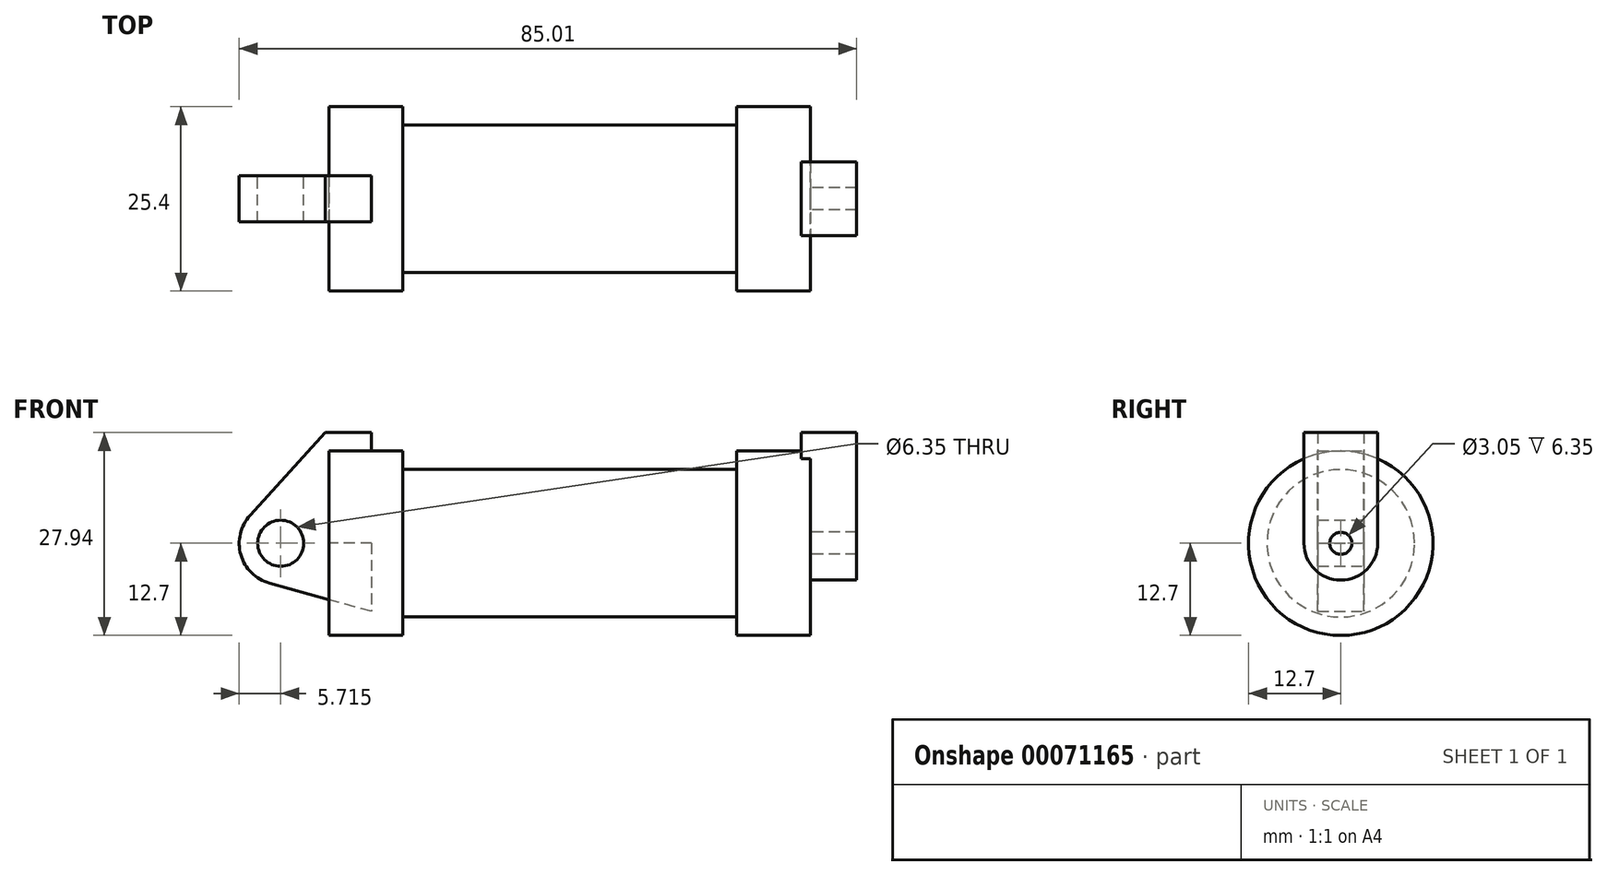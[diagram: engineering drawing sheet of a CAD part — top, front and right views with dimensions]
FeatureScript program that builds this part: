
annotation { "Feature Type Name" : "Feature", "Feature Type Description" : "" }
export const myFeature = defineFeature(function(context is Context, id is Id, definition is map)
    precondition{}
    {
        {
            var Q0;
            Q0=qCreatedBy(makeId("Front.planeOp"),FACE);
            var sketch = newSketch(context, id + "F0", { "sketchPlane" : qUnion([Q0])});
            skLineSegment(sketch, "E0", {"start": v(0, 0) * mm, "end": v(0, 12.7) * mm});
            skLineSegment(sketch, "E1", {"start": v(0, 12.7) * mm, "end": v(10.16, 12.7) * mm});
            skLineSegment(sketch, "E2", {"start": v(10.16, 12.7) * mm, "end": v(10.16, 10.16) * mm});
            skLineSegment(sketch, "E3", {"start": v(10.16, 10.16) * mm, "end": v(56.13, 10.16) * mm});
            skLineSegment(sketch, "E4", {"start": v(56.13, 10.16) * mm, "end": v(56.13, 12.7) * mm});
            skLineSegment(sketch, "E5", {"start": v(56.13, 12.7) * mm, "end": v(66.3, 12.7) * mm});
            skLineSegment(sketch, "E6", {"start": v(66.3, 12.7) * mm, "end": v(66.3, 0) * mm});
            skLineSegment(sketch, "E7", {"start": v(66.3, 0) * mm, "end": v(0, 0) * mm});
            skLineSegment(sketch, "E8", {"start": v(5.84, 15.24) * mm, "end": v(-0.5, 15.24) * mm});
            skLineSegment(sketch, "E9", {"start": v(-0.5, 15.24) * mm, "end": v(-10.88, 3.85) * mm});
            skLineSegment(sketch, "E10", {"start": v(0, 0) * mm, "end": v(-6.65, 0) * mm});
            skCircle(sketch, "E11", {"center": v(-6.65, 0) * mm, "radius": 5.72 * mm});
            skCircle(sketch, "E12", {"center": v(-6.65, 0) * mm, "radius": 3.18 * mm});
            skLineSegment(sketch, "E13", {"start": v(5.84, 15.24) * mm, "end": v(5.84, -9.4) * mm});
            skLineSegment(sketch, "E14", {"start": v(5.84, -9.4) * mm, "end": v(-8.18, -5.5) * mm});
            skSolve(sketch);
        }
        {
            var Q0;
            {var subQ0=sQuery(id+"F0.wireOp",EDGE,"E2");Q0=makeQuery(id+"F0.imprint","IMPRINT",FACE,{"disambiguationData":[TD([[makeQuery(id+"F0.imprint","IMPRINT",EDGE,{"derivedFrom":subQ0}),-1.0]])]});}
            var Q1;
            {var subQ0=sQuery(id+"F0.wireOp",EDGE,"E0");Q1=makeQuery(id+"F0.imprint","IMPRINT",FACE,{"disambiguationData":[TD([[makeQuery(id+"F0.imprint","IMPRINT",EDGE,{"derivedFrom":subQ0}),-1.0]])]});}
            var Q2;
            Q2=sQuery(id+"F0.wireOp",EDGE,"E7");
            revolve(context, id + "F1", {"entities" : qUnion([Q0, Q1]), "axis" : qUnion([Q2]), "revolveType" : RevolveType.FULL});
        }
        {
            var Q0;
            {var subQ3=sQuery(id+"F0.wireOp",EDGE,"E0");Q0=makeQuery(id+"F0.imprint","IMPRINT",FACE,{"disambiguationData":[TD([[makeQuery(id+"F0.imprint","IMPRINT",EDGE,{"derivedFrom":subQ3}),1.0]])]});}
            var Q1;
            {var subQ0=sQuery(id+"F0.wireOp",EDGE,"E14");Q1=makeQuery(id+"F0.imprint","IMPRINT",FACE,{"disambiguationData":[TD([[makeQuery(id+"F0.imprint","IMPRINT",EDGE,{"derivedFrom":subQ0}),-1.0]])]});}
            var Q2;
            {var subQ4=sQuery(id+"F0.wireOp",EDGE,"E12");Q2=makeQuery(id+"F0.imprint","IMPRINT",FACE,{"disambiguationData":[TD([[makeQuery(id+"F0.imprint","IMPRINT",EDGE,{"derivedFrom":subQ4}),-1.0]])]});}
            extrude(context, id + "F2", {"entities" : qUnion([Q0, Q1, Q2]), "depth" : 3.17 * mm, "hasSecondDirection" : true, "secondDirectionOppositeDirection" : true, "secondDirectionDepth" : 3.17 * mm});
        }
        {
            var Q0;
            Q0=makeQuery(id+"F1.opRevolve","SWEPT_FACE",FACE,{"disambiguationData":[OSD([sQuery(id+"F0.wireOp",EDGE,"E6")])]});
            var sketch = newSketch(context, id + "F3", { "sketchPlane" : qUnion([Q0])});
            skCircle(sketch, "E15", {"center": v(0, 0) * mm, "radius": 5.08 * mm});
            skCircle(sketch, "E16", {"center": v(0, 0) * mm, "radius": 1.52 * mm});
            skLineSegment(sketch, "E17", {"start": v(5.08, 0) * mm, "end": v(5.08, 15.24) * mm});
            skLineSegment(sketch, "E18", {"start": v(-5.08, 0) * mm, "end": v(-5.08, 15.24) * mm});
            skLineSegment(sketch, "E19", {"start": v(-5.08, 15.24) * mm, "end": v(5.08, 15.24) * mm});
            skSolve(sketch);
        }
        {
            var Q0;
            {var subQ0=sQuery(id+"F3.wireOp",EDGE,"E19");Q0=makeQuery(id+"F3.imprint","IMPRINT",FACE,{"disambiguationData":[TD([[makeQuery(id+"F3.imprint","IMPRINT",EDGE,{"derivedFrom":subQ0}),-1.0]])]});}
            var Q1;
            {var subQ0=sQuery(id+"F3.wireOp",EDGE,"E17");var subQ1=sQuery(id+"F3.wireOp",EDGE,"E15");var subQ2=makeQuery(id+"F3.imprint","INTERSECT",VERTEX,{"derivedFrom":[subQ1,subQ0]});Q1=makeQuery(id+"F3.imprint","IMPRINT",FACE,{"disambiguationData":[TD([[makeQuery(id+"F3.imprint","IMPRINT",EDGE,{"disambiguationData":[TD([[subQ2,-1.0]])],"derivedFrom":subQ1}),-1.0]])]});}
            var Q2;
            Q2=makeQuery(id+"F3.imprint","IMPRINT",FACE,{"disambiguationData":[TD([[makeQuery(id+"F3.imprint","IMPRINT",EDGE,{"derivedFrom":sQuery(id+"F3.wireOp",EDGE,"E16")}),-1.0]])]});
            extrude(context, id + "F4", {"entities" : qUnion([Q0, Q1, Q2]), "operationType" : NewBodyOperationType.ADD, "depth" : 6.35 * mm, "hasSecondDirection" : true, "secondDirectionOppositeDirection" : true, "secondDirectionDepth" : 1.27 * mm});
        }
        {
            var Q0;
            Q0=makeQuery(id+"F4.boolean.opBoolean","SPLIT",FACE,{"disambiguationData":[TD([makeQuery(id+"F4.opExtrude","SWEPT_FACE",FACE,{"disambiguationData":[OSD([sQuery(id+"F3.wireOp",EDGE,"E16")])]})])],"derivedFrom":makeQuery(id+"F1.opRevolve","SWEPT_FACE",FACE,{"disambiguationData":[OSD([sQuery(id+"F0.wireOp",EDGE,"E6")])]})});
            var Q1;
            Q1=makeQuery(id+"F1.opRevolve","SWEPT_FACE",FACE,{"disambiguationData":[OSD([sQuery(id+"F0.wireOp",EDGE,"E2")])]});
            extrude(context, id + "F5", {"entities" : qUnion([Q0]), "operationType" : NewBodyOperationType.ADD, "endBound" : BoundingType.UP_TO_SURFACE, "oppositeDirection" : true, "endBoundEntityFace" : qUnion([Q1]), "depth" : 25.4 * mm});
        }
    });
